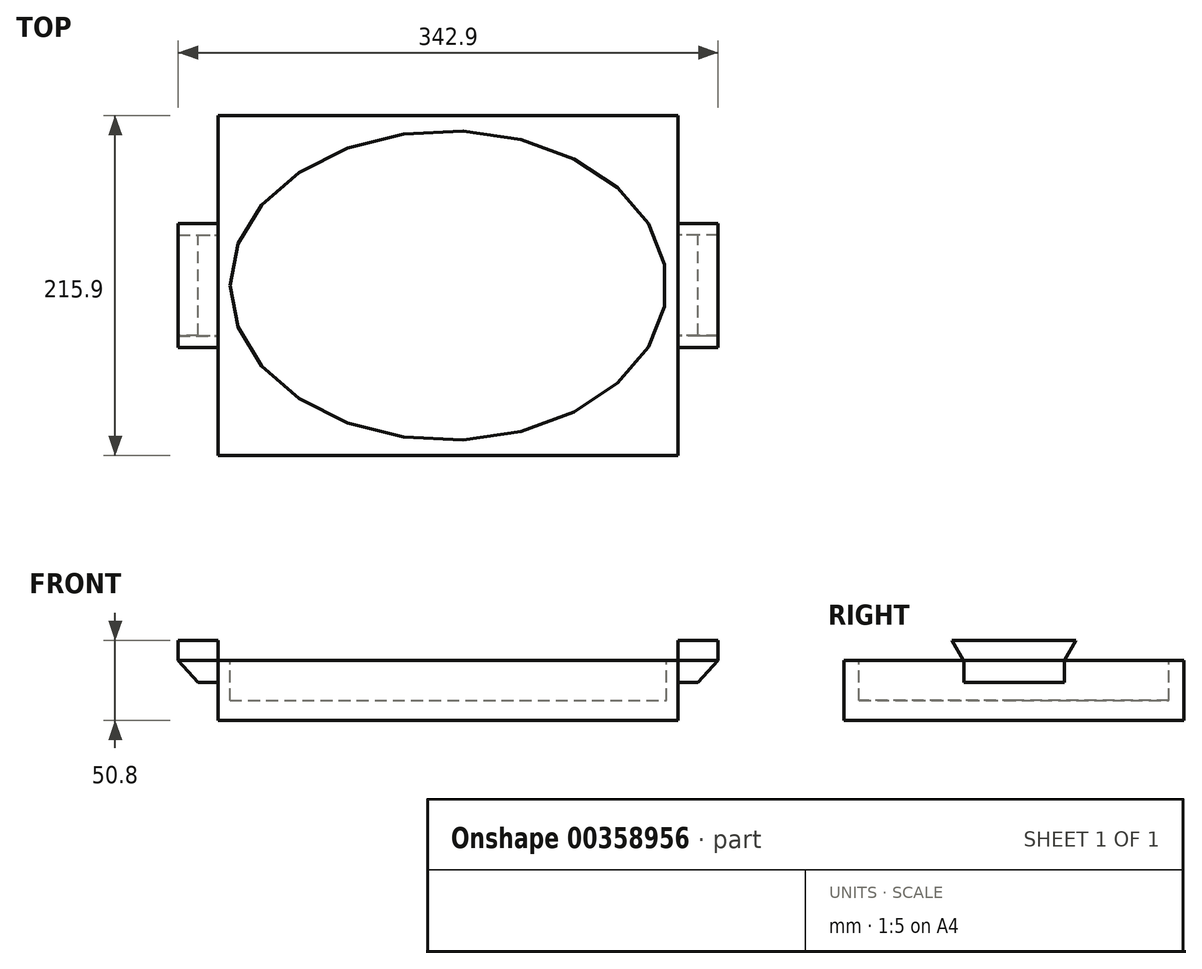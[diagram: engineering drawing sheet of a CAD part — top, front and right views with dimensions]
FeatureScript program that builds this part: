
annotation { "Feature Type Name" : "Feature", "Feature Type Description" : "" }
export const myFeature = defineFeature(function(context is Context, id is Id, definition is map)
    precondition{}
    {
        {
            var Q0;
            Q0=qCreatedBy(makeId("Top.planeOp"),FACE);
            var sketch = newSketch(context, id + "F0", { "sketchPlane" : qUnion([Q0])});
            skLineSegment(sketch, "E0.bottom", {"start": v(-146.05, 107.95) * mm, "end": v(146.05, 107.95) * mm});
            skLineSegment(sketch, "E0.top", {"start": v(-146.05, -107.95) * mm, "end": v(146.05, -107.95) * mm});
            skLineSegment(sketch, "E0.left", {"start": v(-146.05, 107.95) * mm, "end": v(-146.05, -107.95) * mm});
            skLineSegment(sketch, "E0.right", {"start": v(146.05, 107.95) * mm, "end": v(146.05, -107.95) * mm});
            skPoint(sketch, "E0.middle", {"position": v(0, 0) * mm});
            skSolve(sketch);
        }
        {
            var Q0;
            Q0 = qSketchRegion(id + "F0", true);
            extrude(context, id + "F1", {"entities" : qUnion([Q0]), "depth" : 38.1 * mm});
        }
        {
            var Q0;
            Q0=makeQuery(id+"F1.opExtrude","CAP_FACE",FACE,{"disambiguationData":[OSD([sQuery(id+"F0.wireOp",EDGE,"E0.bottom"),sQuery(id+"F0.wireOp",EDGE,"E0.top"),sQuery(id+"F0.wireOp",EDGE,"E0.left"),sQuery(id+"F0.wireOp",EDGE,"E0.right")])],"isStart":false});
            var sketch = newSketch(context, id + "F2", { "sketchPlane" : qUnion([Q0])});
            skEllipse(sketch, "E1", {"center": v(0, 0) * mm, "majorRadius": 138.56 * mm, "minorRadius": 98.34 * mm, "majorAxis": v(-1, 0)});
            skSolve(sketch);
        }
        {
            var Q0;
            Q0 = qSketchRegion(id + "F2", true);
            extrude(context, id + "F3", {"entities" : qUnion([Q0]), "operationType" : NewBodyOperationType.REMOVE, "oppositeDirection" : true, "depth" : 25.4 * mm});
        }
        {
            var Q0;
            Q0=makeQuery(id+"F1.opExtrude","SWEPT_FACE",FACE,{"disambiguationData":[OSD([sQuery(id+"F0.wireOp",EDGE,"E0.left")])]});
            var sketch = newSketch(context, id + "F4", { "sketchPlane" : qUnion([Q0])});
            skPoint(sketch, "E2.endSnap0", {"position": v(0, 38.1) * mm});
            skLineSegment(sketch, "E3", {"start": v(-32.14, 38.1) * mm, "end": v(-39.42, 50.8) * mm});
            skLineSegment(sketch, "E4", {"start": v(-39.42, 50.8) * mm, "end": v(39.42, 50.8) * mm});
            skLineSegment(sketch, "E5", {"start": v(32.14, 38.1) * mm, "end": v(39.42, 50.8) * mm});
            skLineSegment(sketch, "E6", {"start": v(-32.14, 38.1) * mm, "end": v(0, 38.1) * mm});
            skLineSegment(sketch, "E7", {"start": v(32.14, 38.1) * mm, "end": v(0, 38.1) * mm});
            skSolve(sketch);
        }
        {
            var Q0;
            Q0 = qSketchRegion(id + "F4", true);
            extrude(context, id + "F5", {"entities" : qUnion([Q0]), "depth" : 25.4 * mm});
        }
        {
            var Q0;
            Q0=makeQuery(id+"F5.opExtrude","SWEPT_BODY",BODY,{"disambiguationData":[OSD([sQuery(id+"F4.wireOp",EDGE,"E3"),sQuery(id+"F4.wireOp",EDGE,"E4"),sQuery(id+"F4.wireOp",EDGE,"E5"),sQuery(id+"F4.wireOp",EDGE,"E6"),sQuery(id+"F4.wireOp",EDGE,"E7")])]});
            var Q1;
            Q1=qCreatedBy(makeId("Right.planeOp"),FACE);
            mirror(context, id + "F6", {"entities" : qUnion([Q0]), "mirrorPlane" : qUnion([Q1])});
        }
        {
            var Q0;
            Q0=makeQuery(id+"F1.opExtrude","SWEPT_FACE",FACE,{"disambiguationData":[OSD([sQuery(id+"F0.wireOp",EDGE,"E0.left")])]});
            var sketch = newSketch(context, id + "F7", { "sketchPlane" : qUnion([Q0])});
            skLineSegment(sketch, "E8", {"start": v(-32.07, 38.1) * mm, "end": v(31.8, 38.1) * mm});
            skLineSegment(sketch, "E9", {"start": v(31.8, 38.1) * mm, "end": v(31.8, 24) * mm});
            skLineSegment(sketch, "E10", {"start": v(31.8, 24) * mm, "end": v(-32.07, 24) * mm});
            skLineSegment(sketch, "E11", {"start": v(-32.07, 24) * mm, "end": v(-32.07, 38.1) * mm});
            skSolve(sketch);
        }
        {
            var Q0;
            Q0 = qSketchRegion(id + "F7", true);
            extrude(context, id + "F8", {"entities" : qUnion([Q0]), "depth" : 25.4 * mm});
        }
        {
            var Q0;
            Q0=makeQuery(id+"F8.opExtrude","SWEPT_FACE",FACE,{"disambiguationData":[OSD([sQuery(id+"F7.wireOp",EDGE,"E11")])]});
            var sketch = newSketch(context, id + "F9", { "sketchPlane" : qUnion([Q0])});
            skLineSegment(sketch, "E12", {"start": v(171.45, 38.1) * mm, "end": v(158.75, 24) * mm});
            skLineSegment(sketch, "E13", {"start": v(158.75, 24) * mm, "end": v(171.45, 24) * mm});
            skLineSegment(sketch, "E14", {"start": v(171.45, 24) * mm, "end": v(171.45, 38.1) * mm});
            skSolve(sketch);
        }
        {
            var Q0;
            Q0 = qSketchRegion(id + "F9", true);
            extrude(context, id + "F10", {"entities" : qUnion([Q0]), "operationType" : NewBodyOperationType.REMOVE, "oppositeDirection" : true, "depth" : 127 * mm});
        }
        {
            var Q0;
            Q0=makeQuery(id+"F8.opExtrude","SWEPT_BODY",BODY,{"disambiguationData":[OSD([sQuery(id+"F7.wireOp",EDGE,"E8"),sQuery(id+"F7.wireOp",EDGE,"E9"),sQuery(id+"F7.wireOp",EDGE,"E10"),sQuery(id+"F7.wireOp",EDGE,"E11")])]});
            var Q1;
            Q1=qCreatedBy(makeId("Right.planeOp"),FACE);
            mirror(context, id + "F11", {"entities" : qUnion([Q0]), "mirrorPlane" : qUnion([Q1])});
        }
    });
